# Revit family: QF_BOURGEAT_3GN_bain_marie mobile_avec_etuve_cuve_separees
name_source: partatom
category: Equipement spécialisé
revit_build: Autodesk Revit 2015 (Build: 20140606_1530(x64)
units: mm (PartAtom-declared; Revit-internal decimal feet)

## types (2) — shared parameters
Charge max = 150.00 kg
Diamètre de Raccordement Evacuation = 27 mm
Fabricant = BOURGEAT
Fréquence = 50 Hz
Indice de protection = 33
Intensité nominale = 12 A
Longueur hors tout = 1280 mm  [stored 4.19948 ft]
Nature isolant = 30mm laine de roche
Phase = 2
Profondeur hors tout = 695 mm  [stored 2.28018 ft]
Puissance électrique  = 2655 W
Spécification du Fabricant = bain-marie mobiles
Tension = 230 V
URL catalogue = http://www.bourgeat.fr

## per-type parameters (varying)
| type | Hauteur hors tout | Modèle | Poids net à vide | couvercle |
| bain_marie_mobile3GN_avec_couvercle | 950 mm  [stored 3.1168 ft] | 872213 | 105.00 kg | Oui |
| bain_marie_mobile3GN_sans_couvercle | 900 mm  [stored 2.95276 ft] | 872113 | 95.00 kg | Non |

note: [stored X ft] marks values corroborated as IEEE doubles in the binary element streams (Revit-internal decimal feet)
